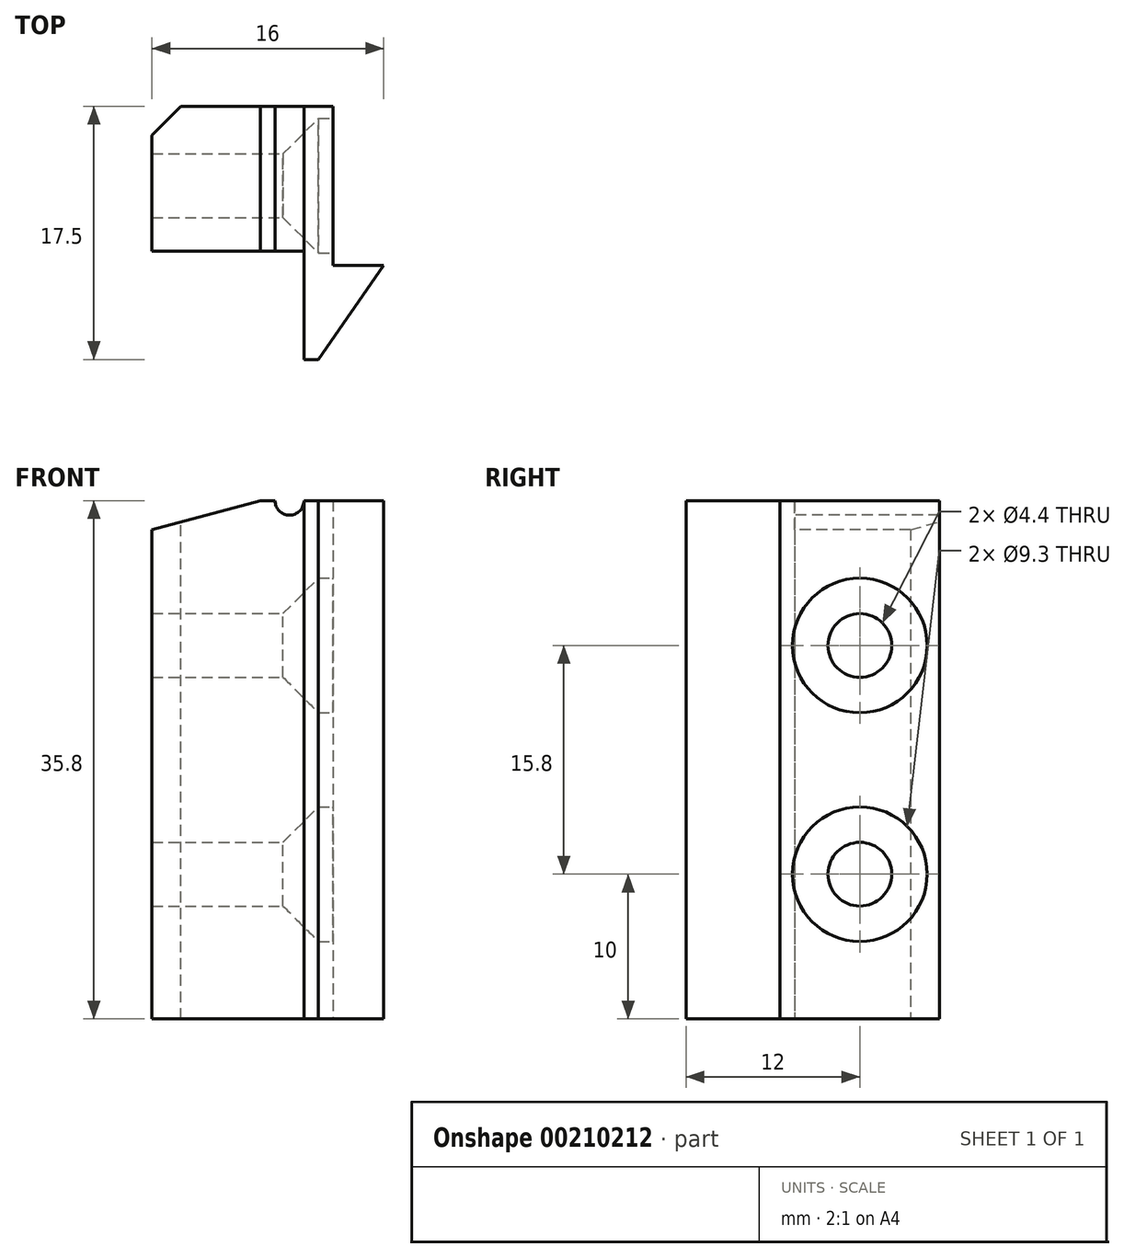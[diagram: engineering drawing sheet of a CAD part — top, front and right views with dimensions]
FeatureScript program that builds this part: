
annotation { "Feature Type Name" : "Feature", "Feature Type Description" : "" }
export const myFeature = defineFeature(function(context is Context, id is Id, definition is map)
    precondition{}
    {
        {
            var Q0;
            Q0=qCreatedBy(makeId("Top.planeOp"),FACE);
            var sketch = newSketch(context, id + "F0", { "sketchPlane" : qUnion([Q0])});
            skLineSegment(sketch, "E0", {"start": v(-10.5, 10) * mm, "end": v(-10.5, 0) * mm});
            skLineSegment(sketch, "E1", {"start": v(-10.5, 0) * mm, "end": v(0, 0) * mm});
            skLineSegment(sketch, "E2", {"start": v(0, 0) * mm, "end": v(0, -7.5) * mm});
            skLineSegment(sketch, "E3", {"start": v(1, -7.5) * mm, "end": v(5.5, -1) * mm});
            skLineSegment(sketch, "E4", {"start": v(5.5, -1) * mm, "end": v(2, -1) * mm});
            skLineSegment(sketch, "E5", {"start": v(2, -1) * mm, "end": v(2, 10) * mm});
            skLineSegment(sketch, "E6", {"start": v(2, 10) * mm, "end": v(-10.5, 10) * mm});
            skLineSegment(sketch, "E7", {"start": v(0, -7.5) * mm, "end": v(1, -7.5) * mm});
            skPoint(sketch, "E8.orphan", {"position": v(0, -8.94) * mm});
            skSolve(sketch);
        }
        {
            var Q0;
            Q0 = qSketchRegion(id + "F0", true);
            extrude(context, id + "F1", {"entities" : qUnion([Q0]), "depth" : 40 * mm});
        }
        {
            var Q0;
            Q0=makeQuery(id+"F1.opExtrude","SWEPT_FACE",FACE,{"disambiguationData":[OSD([sQuery(id+"F0.wireOp",EDGE,"E1")])]});
            var sketch = newSketch(context, id + "F2", { "sketchPlane" : qUnion([Q0])});
            skLineSegment(sketch, "E9", {"start": v(0, 35.8) * mm, "end": v(5.5, 35.8) * mm});
            skLineSegment(sketch, "E10", {"start": v(5.5, 35.8) * mm, "end": v(5.5, 40) * mm});
            skLineSegment(sketch, "E11", {"start": v(5.5, 40) * mm, "end": v(-10.5, 40) * mm});
            skLineSegment(sketch, "E12", {"start": v(-10.5, 40) * mm, "end": v(-10.5, 33.8) * mm});
            skArc(sketch, "E13", {"start": v(-2, 35.8) * mm, "mid": v(-1, 34.8) * mm, "end": v(0, 35.8) * mm});
            skLineSegment(sketch, "E14", {"start": v(-2, 35.8) * mm, "end": v(-3, 35.8) * mm});
            skLineSegment(sketch, "E15", {"start": v(-3, 35.8) * mm, "end": v(-10.5, 33.8) * mm});
            skSolve(sketch);
        }
        {
            var Q0;
            Q0 = qSketchRegion(id + "F2", true);
            extrude(context, id + "F3", {"entities" : qUnion([Q0]), "operationType" : NewBodyOperationType.REMOVE, "endBound" : BoundingType.SYMMETRIC, "oppositeDirection" : true, "depth" : 25 * mm});
        }
        {
            var Q0;
            Q0=makeQuery(id+"F1.opExtrude","SWEPT_FACE",FACE,{"disambiguationData":[OSD([sQuery(id+"F0.wireOp",EDGE,"E5")])]});
            var sketch = newSketch(context, id + "F4", { "sketchPlane" : qUnion([Q0])});
            skCircle(sketch, "E16", {"center": v(4.5, 25.8) * mm, "radius": 2.2 * mm});
            skCircle(sketch, "E17", {"center": v(4.5, 10) * mm, "radius": 2.2 * mm});
            skSolve(sketch);
        }
        {
            var Q0;
            Q0 = qSketchRegion(id + "F4", true);
            extrude(context, id + "F5", {"entities" : qUnion([Q0]), "operationType" : NewBodyOperationType.REMOVE, "endBound" : BoundingType.THROUGH_ALL, "oppositeDirection" : true, "depth" : 25 * mm});
        }
        {
            var Q0;
            Q0=makeQuery(id+"F1.opExtrude","SWEPT_FACE",FACE,{"disambiguationData":[OSD([sQuery(id+"F0.wireOp",EDGE,"E5")])]});
            var sketch = newSketch(context, id + "F6", { "sketchPlane" : qUnion([Q0])});
            skCircle(sketch, "E18", {"center": v(4.5, 25.8) * mm, "radius": 4.65 * mm});
            skCircle(sketch, "E19", {"center": v(4.5, 10) * mm, "radius": 4.65 * mm});
            skSolve(sketch);
        }
        {
            var Q0;
            Q0=makeQuery(id+"F1.opExtrude","SWEPT_EDGE",EDGE,{"disambiguationData":[OSD([sQuery(id+"F0.wireOp",EDGE,"E0"),sQuery(id+"F0.wireOp",EDGE,"E6")])]});
            chamfer(context, id + "F7", {"entities" : qUnion([Q0]), "width" : 2 * mm, "tangentPropagation" : true});
        }
        {
            var Q0;
            Q0 = qSketchRegion(id + "F6", true);
            extrude(context, id + "F8", {"entities" : qUnion([Q0]), "operationType" : NewBodyOperationType.REMOVE, "oppositeDirection" : true, "depth" : 1 * mm});
        }
        {
            var Q0;
            Q0=makeQuery(id+"F8.boolean.opBoolean","INTERSECT",EDGE,{"derivedFrom":[makeQuery(id+"F5.boolean.opBoolean","COPY",FACE,{"derivedFrom":makeQuery(id+"F5.opExtrude","SWEPT_FACE",FACE,{"disambiguationData":[OSD([sQuery(id+"F4.wireOp",EDGE,"E16")])]})}),makeQuery(id+"F8.opExtrude","CAP_FACE",FACE,{"disambiguationData":[OSD([sQuery(id+"F6.wireOp",EDGE,"E18")])],"isStart":false})]});
            var Q1;
            Q1=makeQuery(id+"F8.boolean.opBoolean","INTERSECT",EDGE,{"derivedFrom":[makeQuery(id+"F5.boolean.opBoolean","COPY",FACE,{"derivedFrom":makeQuery(id+"F5.opExtrude","SWEPT_FACE",FACE,{"disambiguationData":[OSD([sQuery(id+"F4.wireOp",EDGE,"E17")])]})}),makeQuery(id+"F8.opExtrude","CAP_FACE",FACE,{"disambiguationData":[OSD([sQuery(id+"F6.wireOp",EDGE,"E19")])],"isStart":false})]});
            chamfer(context, id + "F9", {"entities" : qUnion([Q0, Q1]), "width" : 2.45 * mm, "tangentPropagation" : true});
        }
    });
